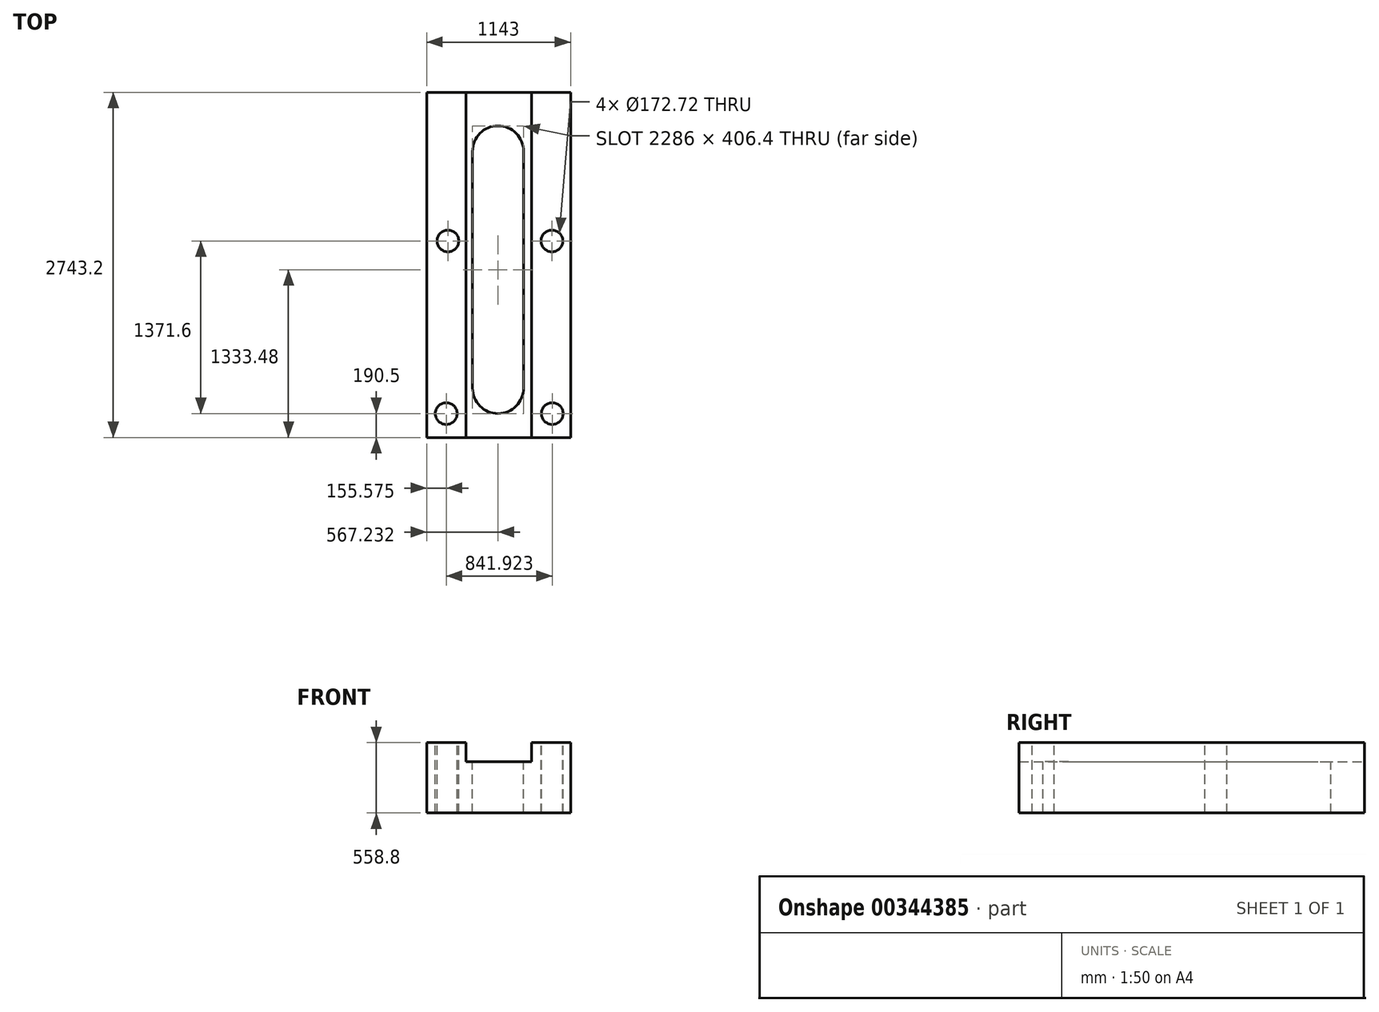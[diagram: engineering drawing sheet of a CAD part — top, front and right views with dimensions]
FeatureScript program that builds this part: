
annotation { "Feature Type Name" : "Feature", "Feature Type Description" : "" }
export const myFeature = defineFeature(function(context is Context, id is Id, definition is map)
    precondition{}
    {
        {
            var Q0;
            Q0=qCreatedBy(makeId("Front.planeOp"),FACE);
            var sketch = newSketch(context, id + "F0", { "sketchPlane" : qUnion([Q0])});
            skLineSegment(sketch, "E0.bottom", {"start": v(571.5, 279.4) * mm, "end": v(260.35, 279.4) * mm});
            skLineSegment(sketch, "E0.top", {"start": v(571.5, -279.4) * mm, "end": v(-571.5, -279.4) * mm});
            skLineSegment(sketch, "E0.left", {"start": v(571.5, 279.4) * mm, "end": v(571.5, -279.4) * mm});
            skLineSegment(sketch, "E0.right", {"start": v(-571.5, 279.4) * mm, "end": v(-571.5, -279.4) * mm});
            skPoint(sketch, "E0.middle", {"position": v(0, 0) * mm});
            skLineSegment(sketch, "E1", {"start": v(-260.35, 279.4) * mm, "end": v(-260.35, 127) * mm});
            skLineSegment(sketch, "E2", {"start": v(-260.35, 127) * mm, "end": v(260.35, 127) * mm});
            skLineSegment(sketch, "E3", {"start": v(260.35, 127) * mm, "end": v(260.35, 279.4) * mm});
            skLineSegment(sketch, "E4.trimOffspring", {"start": v(-260.35, 279.4) * mm, "end": v(-571.5, 279.4) * mm});
            skSolve(sketch);
        }
        {
            var Q0;
            Q0=makeQuery(id+"F0.imprint","IMPRINT",FACE,{"disambiguationData":[TD([[makeQuery(id+"F0.imprint","IMPRINT",EDGE,{"derivedFrom":sQuery(id+"F0.wireOp",EDGE,"E0.bottom")}),1.0]])]});
            extrude(context, id + "F1", {"entities" : qUnion([Q0]), "depth" : 2743.2 * mm});
        }
        {
            var Q0;
            Q0=makeQuery(id+"F1.opExtrude","SWEPT_FACE",FACE,{"disambiguationData":[OSD([sQuery(id+"F0.wireOp",EDGE,"E2")])]});
            var sketch = newSketch(context, id + "F2", { "sketchPlane" : qUnion([Q0])});
            skLineSegment(sketch, "E5", {"start": v(-207.47, -469.92) * mm, "end": v(-207.47, -2349.52) * mm});
            skLineSegment(sketch, "E6", {"start": v(198.93, -2349.52) * mm, "end": v(198.93, -469.92) * mm});
            skArc(sketch, "E7", {"start": v(198.93, -469.92) * mm, "mid": v(-4.27, -266.72) * mm, "end": v(-207.47, -469.92) * mm});
            skArc(sketch, "E8", {"start": v(-207.47, -2349.52) * mm, "mid": v(-4.27, -2552.72) * mm, "end": v(198.93, -2349.52) * mm});
            skSolve(sketch);
        }
        {
            var Q0;
            Q0 = qSketchRegion(id + "F2", true);
            extrude(context, id + "F3", {"entities" : qUnion([Q0]), "operationType" : NewBodyOperationType.REMOVE, "oppositeDirection" : true, "depth" : 406.4 * mm});
        }
        {
            var Q0;
            Q0=makeQuery(id+"F1.opExtrude","SWEPT_FACE",FACE,{"disambiguationData":[OSD([sQuery(id+"F0.wireOp",EDGE,"E4.trimOffspring")])]});
            var sketch = newSketch(context, id + "F4", { "sketchPlane" : qUnion([Q0])});
            skCircle(sketch, "E9", {"center": v(-415.93, -2552.7) * mm, "radius": 86.36 * mm});
            skPoint(sketch, "E9.centerSnap0", {"position": v(-415.93, -2743.2) * mm});
            skCircle(sketch, "E10", {"center": v(-402.45, -1181.1) * mm, "radius": 86.36 * mm});
            skCircle(sketch, "E11", {"center": v(423.18, -1181.1) * mm, "radius": 86.36 * mm});
            skCircle(sketch, "E12", {"center": v(426, -2552.7) * mm, "radius": 86.36 * mm});
            skSolve(sketch);
        }
        {
            var Q0;
            Q0=makeQuery(id+"F4.imprint","IMPRINT",FACE,{"disambiguationData":[TD([[makeQuery(id+"F4.imprint","IMPRINT",EDGE,{"derivedFrom":sQuery(id+"F4.wireOp",EDGE,"E10")}),1.0]])]});
            var Q1;
            Q1=makeQuery(id+"F4.imprint","IMPRINT",FACE,{"disambiguationData":[TD([[makeQuery(id+"F4.imprint","IMPRINT",EDGE,{"derivedFrom":sQuery(id+"F4.wireOp",EDGE,"E9")}),1.0]])]});
            var Q2;
            Q2=makeQuery(id+"F4.imprint","IMPRINT",FACE,{"disambiguationData":[TD([[makeQuery(id+"F4.imprint","IMPRINT",EDGE,{"derivedFrom":sQuery(id+"F4.wireOp",EDGE,"E12")}),1.0]])]});
            var Q3;
            Q3=makeQuery(id+"F4.imprint","IMPRINT",FACE,{"disambiguationData":[TD([[makeQuery(id+"F4.imprint","IMPRINT",EDGE,{"derivedFrom":sQuery(id+"F4.wireOp",EDGE,"E11")}),1.0]])]});
            extrude(context, id + "F5", {"entities" : qUnion([Q0, Q1, Q2, Q3]), "operationType" : NewBodyOperationType.REMOVE, "oppositeDirection" : true, "depth" : 558.8 * mm});
        }
    });
